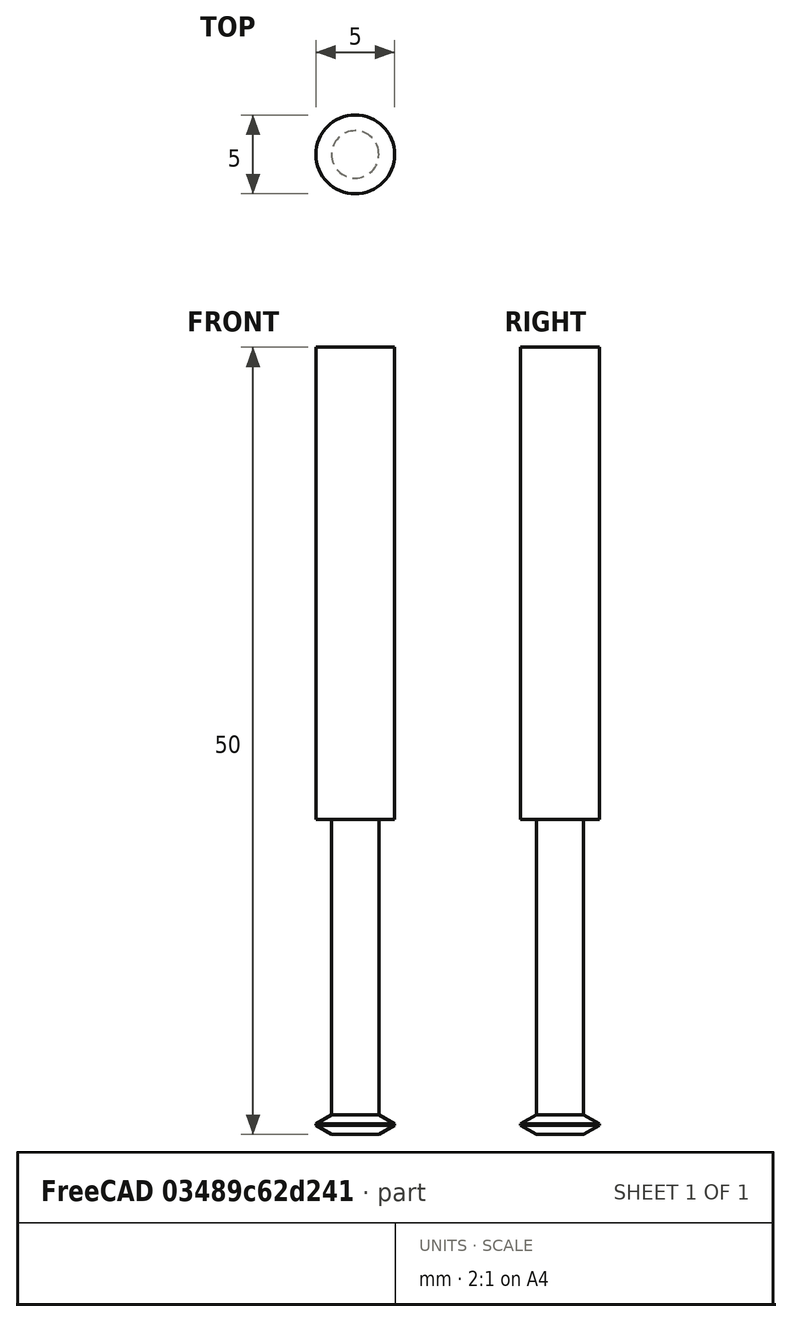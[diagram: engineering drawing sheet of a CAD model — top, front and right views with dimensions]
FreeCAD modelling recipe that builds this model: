
FCSTD DOCUMENT  (FreeCAD 1.0R39109 (Git))
Label: thread-mill
License: Creative Commons Attribution 4.0
LicenseURL: https://creativecommons.org/licenses/by/4.0/
objects: Sketcher::SketchObject×1, PartDesign::Revolution×1, App::FeaturePython×1, PartDesign::Body×1
note: 6 computed .brp shape members not serialized (recipe doc carries the construction recipe); baked Part::Feature solids carry a one-line shape summary decoded from their .brp

FEATURE [Sketcher::SketchObject] Sketch
  ArcFitTolerance = 0
  AttachmentSupport = -> [XZ_Plane]
  FullyConstrained = true
  MakeInternals = false
  MapMode = 5
  Placement = pos=(0,0,0) rot=(1,0,0;1.5708rad)
  expr: Constraints[15] = <<Attributes>>.cuttingAngle
  expr: Constraints[18] = <<Attributes>>.Diameter
  expr: Constraints[19] = <<Attributes>>.cuttingAngle
  expr: Constraints[21] = max(<<Attributes>>.Crest; <<Attributes>>.ShankDiameter / 10000)
  expr: Constraints[27] = <<Attributes>>.NeckLength
  expr: Constraints[30] = <<Attributes>>.NeckDiameter
  expr: Constraints[5] = <<Attributes>>.Length
  expr: Constraints[8] = <<Attributes>>.ShankDiameter
  sketch-geometry (12):
    g0: LineSegment StartX=0 StartY=50 StartZ=0 EndX=0 EndY=0 EndZ=0
    g1: LineSegment StartX=0 StartY=0 StartZ=0 EndX=1.5 EndY=0 EndZ=0
    g2: LineSegment StartX=2.5 StartY=50 StartZ=0 EndX=0 EndY=50 EndZ=0
    g3: LineSegment StartX=1.5 StartY=1.2547 StartZ=0 EndX=2.5 EndY=0.67735 EndZ=0
    g4: LineSegment StartX=1.5 StartY=20 StartZ=0 EndX=1.5 EndY=1.2547 EndZ=0
    g5: LineSegment [constr] StartX=-2.5 StartY=50 StartZ=0 EndX=2.5 EndY=50 EndZ=0
    g6: LineSegment StartX=2.5 StartY=0.67735 StartZ=0 EndX=2.5 EndY=0.57735 EndZ=0
    g7: LineSegment StartX=2.5 StartY=0.57735 StartZ=0 EndX=1.5 EndY=0 EndZ=0
    g8: LineSegment [constr] StartX=2.5 StartY=0.57735 StartZ=0 EndX=-2.5 EndY=0.57735 EndZ=0
    g9: LineSegment StartX=2.5 StartY=50 StartZ=0 EndX=2.5 EndY=20.01 EndZ=0
    g10: LineSegment StartX=2.5 StartY=20.01 StartZ=0 EndX=1.5 EndY=20 EndZ=0
    g11: LineSegment [constr] StartX=1.5 StartY=20 StartZ=0 EndX=-1.5 EndY=20 EndZ=0
  constraints (32):
    c: Vertical(g0)
    c: Coincident(g0,g1)
    c: Horizontal(g1)
    c: Horizontal(g2)
    c: Coincident(g0,g2)
    c: DistanceY(g1,g2) = 50
    c: Vertical(g4)
    c: Symmetric(g5,g5,g0)
    c: DistanceX(g5,g5) = 5
    c: Coincident(g3,g4)
    c: Coincident(g0,g-1)
    c: Coincident(g6,g3)
    c: Vertical(g6)
    c: Coincident(g7,g6)
    c: Coincident(g7,g1)
    c: Angle(g3,g7) = 1.0472
    c: Coincident(g8,g6)
    c: Symmetric(g6,g8,g-2)
    c: DistanceX(g8,g8) = 5
    c: Angle(g-2,g3) = 1.0472
    c: Vertical(g1,g3)
    c: DistanceY(g6,g6) = 0.1
    c: Coincident(g5,g2)
    c: Coincident(g2,g9)
    c: Vertical(g9)
    c: Coincident(g9,g10)
    c: Coincident(g10,g4)
    c: DistanceY(g4) = 20
    c: Coincident(g11,g4)
    c: Symmetric(g4,g11,g0)
    c: DistanceX(g11,g11) = 3
    c: DistanceY(g4,g9) = 0.01
FEATURE [PartDesign::Revolution] Revolution
  AllowMultiFace = false
  Angle = 360
  Angle2 = 60
  Axis = (0,2e-16,1)
  Base = (0,0,0)
  Placement = pos=(0,0,0) rot=(1,0,0;1.5708rad)
  Profile = -> Sketch
  ReferenceAxis = -> Sketch [V_Axis]
  Reversed = true
  Suppressed = false
  Type = 0
FEATURE [App::FeaturePython] PropertyBag  label="Attributes"  # WARN: FeaturePython — macro-defined, semantics opaque (R4)
  Crest = 0.1
  CustomPropertyGroups = 0
  Diameter = 5
  Flutes = 4
  Length = 50
  NeckDiameter = 3
  NeckLength = 20
  ShankDiameter = 5
  cuttingAngle = 60
FEATURE [PartDesign::Body] Body  label="ThreadMill"
  AllowCompound = false
  Group = -> [Sketch,Revolution,PropertyBag]
  Origin = -> Origin
  Tip = -> Revolution
